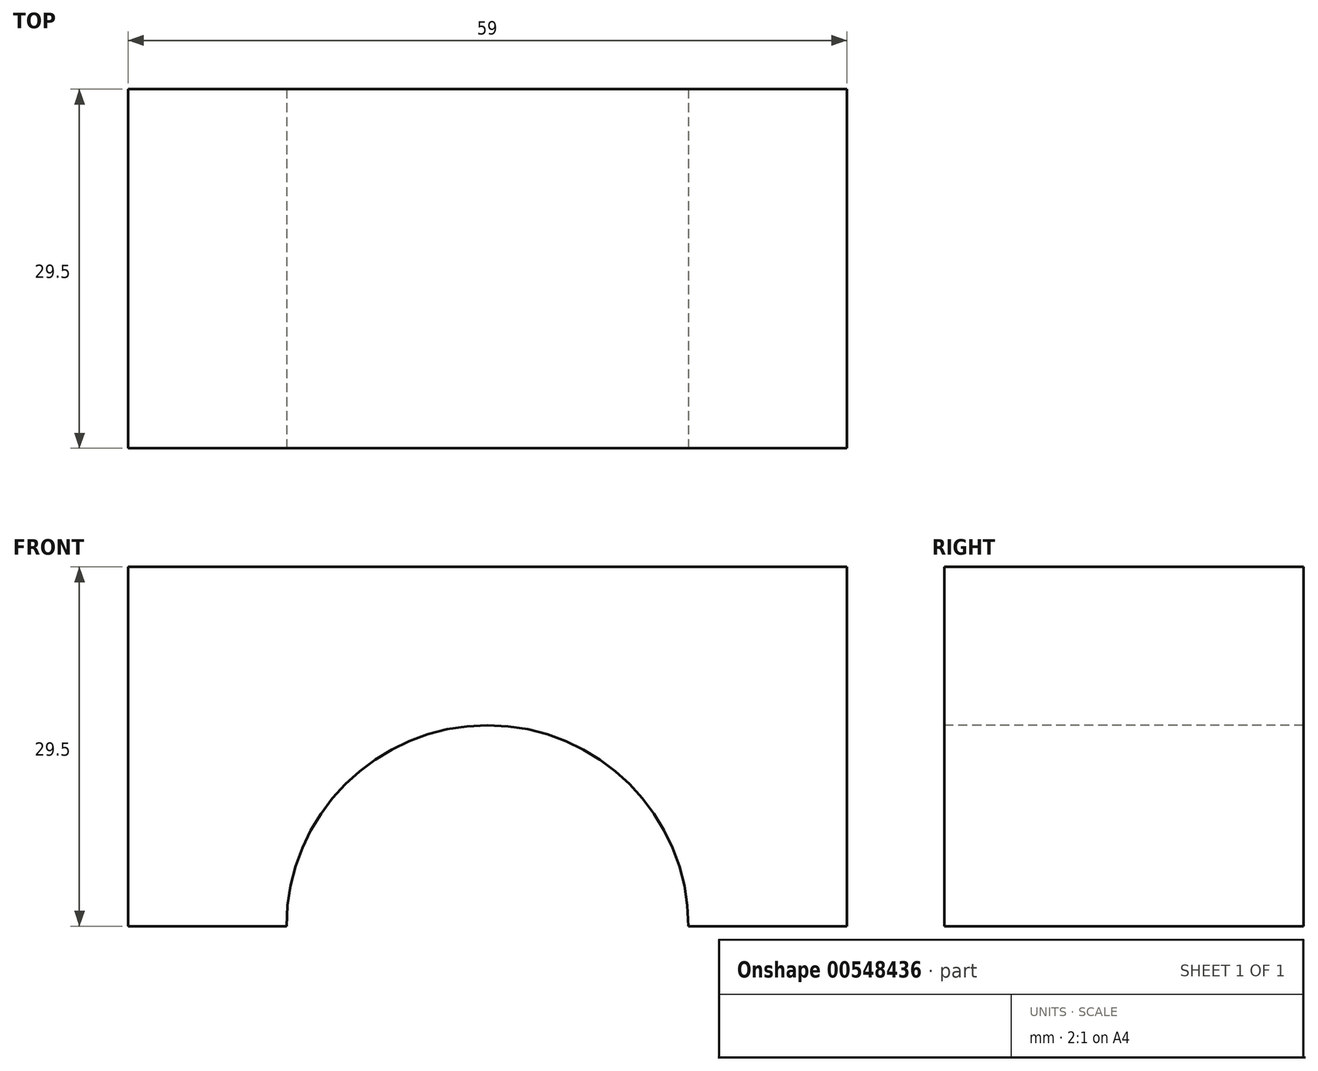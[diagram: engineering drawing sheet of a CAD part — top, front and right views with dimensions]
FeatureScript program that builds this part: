
annotation { "Feature Type Name" : "Feature", "Feature Type Description" : "" }
export const myFeature = defineFeature(function(context is Context, id is Id, definition is map)
    precondition{}
    {
        {
            var Q0;
            Q0=qCreatedBy(makeId("Front.planeOp"),FACE);
            var sketch = newSketch(context, id + "F0", { "sketchPlane" : qUnion([Q0])});
            skLineSegment(sketch, "E0.bottom", {"start": v(29.5, 29.5) * mm, "end": v(-29.5, 29.5) * mm});
            skLineSegment(sketch, "E0.top", {"start": v(29.5, -29.5) * mm, "end": v(-29.5, -29.5) * mm});
            skLineSegment(sketch, "E0.left", {"start": v(29.5, 29.5) * mm, "end": v(29.5, -29.5) * mm});
            skLineSegment(sketch, "E0.right", {"start": v(-29.5, 29.5) * mm, "end": v(-29.5, -29.5) * mm});
            skPoint(sketch, "E0.middle", {"position": v(0, 0) * mm});
            skSolve(sketch);
        }
        {
            var Q0;
            Q0=makeQuery(id+"F0.imprint","IMPRINT",FACE,{"disambiguationData":[TD([[makeQuery(id+"F0.imprint","IMPRINT",EDGE,{"derivedFrom":sQuery(id+"F0.wireOp",EDGE,"E0.bottom")}),1.0]])]});
            extrude(context, id + "F1", {"entities" : qUnion([Q0]), "depth" : 29.5 * mm, "offsetDistance" : 25 * mm});
        }
        {
            var Q0;
            Q0=makeQuery(id+"F1.opExtrude","CAP_FACE",FACE,{"disambiguationData":[OSD([sQuery(id+"F0.wireOp",EDGE,"E0.bottom"),sQuery(id+"F0.wireOp",EDGE,"E0.top"),sQuery(id+"F0.wireOp",EDGE,"E0.left"),sQuery(id+"F0.wireOp",EDGE,"E0.right")])],"isStart":false});
            var sketch = newSketch(context, id + "F2", { "sketchPlane" : qUnion([Q0])});
            skCircle(sketch, "E1", {"center": v(0, 0) * mm, "radius": 16.5 * mm});
            skLineSegment(sketch, "E2", {"start": v(-29.5, 0) * mm, "end": v(29.5, 0) * mm});
            skLineSegment(sketch, "E3", {"start": v(29.5, 0) * mm, "end": v(29.5, -29.5) * mm});
            skLineSegment(sketch, "E4", {"start": v(29.5, -29.5) * mm, "end": v(-29.5, -29.5) * mm});
            skLineSegment(sketch, "E5", {"start": v(-29.5, -29.5) * mm, "end": v(-29.5, 0) * mm});
            skSolve(sketch);
        }
        {
            var Q0;
            Q0=makeQuery(id+"F2.imprint","IMPRINT",FACE,{"disambiguationData":[TD([[makeQuery(id+"F2.imprint","IMPRINT",EDGE,{"derivedFrom":sQuery(id+"F2.wireOp",EDGE,"E1")}),1.0]])]});
            extrude(context, id + "F3", {"entities" : qUnion([Q0]), "operationType" : NewBodyOperationType.REMOVE, "endBound" : BoundingType.THROUGH_ALL, "oppositeDirection" : true, "depth" : 25 * mm, "offsetDistance" : 25 * mm});
        }
        {
            var Q0;
            Q0 = qSketchRegion(id + "F2", true);
            extrude(context, id + "F4", {"entities" : qUnion([Q0]), "operationType" : NewBodyOperationType.REMOVE, "endBound" : BoundingType.THROUGH_ALL, "oppositeDirection" : true, "depth" : 25 * mm, "offsetDistance" : 25 * mm});
        }
    });
